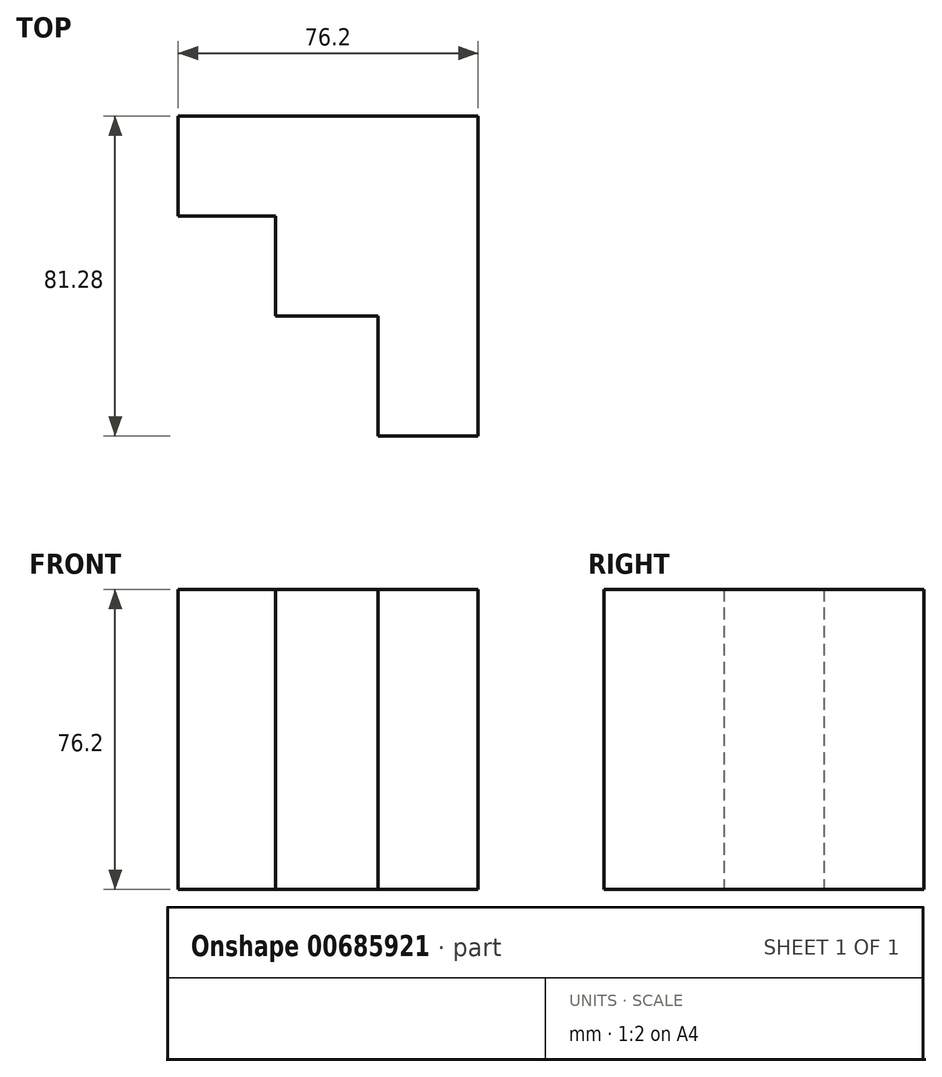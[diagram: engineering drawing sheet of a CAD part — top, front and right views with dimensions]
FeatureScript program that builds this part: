
annotation { "Feature Type Name" : "Feature", "Feature Type Description" : "" }
export const myFeature = defineFeature(function(context is Context, id is Id, definition is map)
    precondition{}
    {
        {
            var Q0;
            Q0=qCreatedBy(makeId("Top.planeOp"),FACE);
            var sketch = newSketch(context, id + "F0", { "sketchPlane" : qUnion([Q0])});
            skLineSegment(sketch, "E0", {"start": v(0, 0) * mm, "end": v(0, 25.4) * mm});
            skLineSegment(sketch, "E1", {"start": v(0, 25.4) * mm, "end": v(-50.8, 25.4) * mm});
            skLineSegment(sketch, "E2", {"start": v(-50.8, 25.4) * mm, "end": v(-50.8, 0) * mm});
            skLineSegment(sketch, "E3", {"start": v(-50.8, 0) * mm, "end": v(0, 0) * mm});
            skSolve(sketch);
        }
        {
            var Q0;
            Q0 = qSketchRegion(id + "F0", true);
            extrude(context, id + "F1", {"entities" : qUnion([Q0]), "depth" : 25.4 * mm, "offsetDistance" : 25.4 * mm});
        }
        {
            var Q0;
            Q0=qCreatedBy(makeId("Top.planeOp"),FACE);
            var sketch = newSketch(context, id + "F2", { "sketchPlane" : qUnion([Q0])});
            skLineSegment(sketch, "E4", {"start": v(-26.07, 0) * mm, "end": v(-26.07, -25.4) * mm});
            skLineSegment(sketch, "E5", {"start": v(-26.07, -25.4) * mm, "end": v(0, -25.4) * mm});
            skLineSegment(sketch, "E6", {"start": v(0, -25.4) * mm, "end": v(0, 0) * mm});
            skLineSegment(sketch, "E7", {"start": v(0, 0) * mm, "end": v(-26.07, 0) * mm});
            skSolve(sketch);
        }
        {
            var Q0;
            Q0 = qSketchRegion(id + "F2", true);
            extrude(context, id + "F3", {"entities" : qUnion([Q0]), "operationType" : NewBodyOperationType.ADD, "depth" : 25.4 * mm, "offsetDistance" : 25.4 * mm});
        }
        {
            var Q0;
            Q0=makeQuery(id+"F3.boolean.opBoolean","MERGE",FACE,{"derivedFrom":[makeQuery(id+"F1.opExtrude","CAP_FACE",FACE,{"disambiguationData":[OSD([sQuery(id+"F0.wireOp",EDGE,"E0"),sQuery(id+"F0.wireOp",EDGE,"E1"),sQuery(id+"F0.wireOp",EDGE,"E2"),sQuery(id+"F0.wireOp",EDGE,"E3")])],"isStart":false}),makeQuery(id+"F3.opExtrude","CAP_FACE",FACE,{"disambiguationData":[OSD([sQuery(id+"F2.wireOp",EDGE,"E4"),sQuery(id+"F2.wireOp",EDGE,"E5"),sQuery(id+"F2.wireOp",EDGE,"E6"),sQuery(id+"F2.wireOp",EDGE,"E7")])],"isStart":false})]});
            var sketch = newSketch(context, id + "F4", { "sketchPlane" : qUnion([Q0])});
            skLineSegment(sketch, "E8", {"start": v(0, 25.4) * mm, "end": v(-50.8, 25.4) * mm});
            skLineSegment(sketch, "E9", {"start": v(-50.8, 25.4) * mm, "end": v(-50.8, 0) * mm});
            skLineSegment(sketch, "E10", {"start": v(-50.8, 0) * mm, "end": v(-26.07, 0) * mm});
            skLineSegment(sketch, "E11", {"start": v(-26.07, 0) * mm, "end": v(-26.07, -25.4) * mm});
            skLineSegment(sketch, "E12", {"start": v(-26.07, -25.4) * mm, "end": v(0, -25.4) * mm});
            skLineSegment(sketch, "E13", {"start": v(0, -25.4) * mm, "end": v(0, 25.4) * mm});
            skSolve(sketch);
        }
        {
            var Q0;
            Q0 = qSketchRegion(id + "F4", true);
            extrude(context, id + "F5", {"entities" : qUnion([Q0]), "operationType" : NewBodyOperationType.ADD, "depth" : 50.8 * mm, "offsetDistance" : 25.4 * mm});
        }
        {
            var Q0;
            Q0=makeQuery(id+"F5.boolean.opBoolean","MERGE",FACE,{"derivedFrom":[makeQuery(id+"F3.boolean.opBoolean","MERGE",FACE,{"derivedFrom":[makeQuery(id+"F1.opExtrude","SWEPT_FACE",FACE,{"disambiguationData":[OSD([sQuery(id+"F0.wireOp",EDGE,"E0")])]}),makeQuery(id+"F3.opExtrude","SWEPT_FACE",FACE,{"disambiguationData":[OSD([sQuery(id+"F2.wireOp",EDGE,"E6")])]})]}),makeQuery(id+"F5.opExtrude","SWEPT_FACE",FACE,{"disambiguationData":[OSD([sQuery(id+"F4.wireOp",EDGE,"E13")])]})]});
            var sketch = newSketch(context, id + "F6", { "sketchPlane" : qUnion([Q0])});
            skLineSegment(sketch, "E14", {"start": v(-25.4, 0) * mm, "end": v(-55.88, 0) * mm});
            skLineSegment(sketch, "E15", {"start": v(-55.88, 0) * mm, "end": v(-55.88, 76.2) * mm});
            skLineSegment(sketch, "E16", {"start": v(-55.88, 76.2) * mm, "end": v(-23.2, 76.2) * mm});
            skLineSegment(sketch, "E17", {"start": v(-23.2, 76.2) * mm, "end": v(25.4, 76.2) * mm});
            skLineSegment(sketch, "E18", {"start": v(25.4, 76.2) * mm, "end": v(25.4, 0) * mm});
            skLineSegment(sketch, "E19", {"start": v(25.4, 0) * mm, "end": v(-25.4, 0) * mm});
            skSolve(sketch);
        }
        {
            var Q0;
            Q0 = qSketchRegion(id + "F6", true);
            extrude(context, id + "F7", {"entities" : qUnion([Q0]), "operationType" : NewBodyOperationType.ADD, "depth" : 25.4 * mm, "offsetDistance" : 25.4 * mm});
        }
    });
